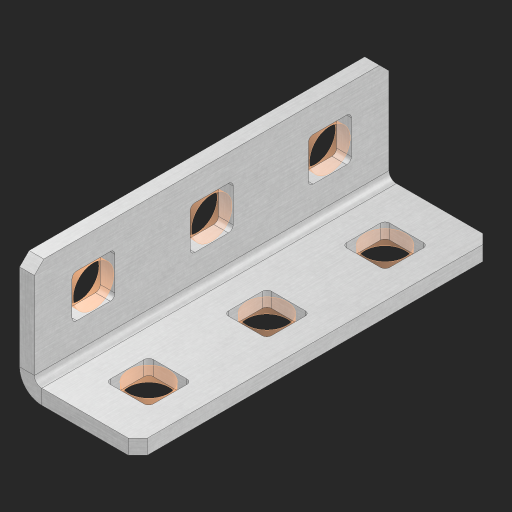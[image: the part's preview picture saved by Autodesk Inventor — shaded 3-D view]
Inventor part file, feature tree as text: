
AUTODESK INVENTOR PART (.ipt)
format: ipt  version: 2023 (Build 270158000, 158)  size: 484,864 bytes
history: native  units: in
note: dims shown in document units (in); Inventor stores cm internally (conversion verified against a paired STEP export)
features: other x12, sheet_metal_op x8, extrude x7, sketch x5, pattern_linear x1, mirror x1, chamfer x1
ambient origin geometry x8: Origin, YZ Plane, XZ Plane, XY Plane, X Axis, Y Axis, Z Axis, Center Point
bodies: Solid1 (feature_tree), Body (feature_tree)
feature tree (35):
  sheet_metal_op  "Flanges"
  sheet_metal_op  "Body Pattern"
  other  "Arc Length"
  pattern_linear  "Notch Pattern"  Spacing1=0.125in  [1 undecoded]
  other  "Diagonal Plane"
  mirror  "Everything Mirrored"
  chamfer  "End Chamfer"
  sketch  "Sketch1"  dims[d0=0.5in]
  other  "Plate1"
  sketch  "Sketch2"  dims[d1=1.5in]
  other  "Plate2"
  sheet_metal_op  "Bend1"
  sheet_metal_op  "Corner1"
  sketch  "Sketch8"  dims[d2=0.0625in]
  sketch  "Sketch9"  dims[d3=0.0625in]
  other  "Srf91"
  sheet_metal_op  "Body Pattern Sketch"
  other  "Srf92"
  sketch  "Sketch13"  dims[d4=0.0312in d5=0.125in d6=0.0625in d7=0.5in d8=90.0deg d9=0.0312in d10=0.25in d11=0.0625in d12=0.0625in d49=0.182in d50=0.02in d52=0.25in d53=0.0625in d54=0.0in d55=0.172in d56=1.0in d57=0.0in d85=0.1473in d86=0.1782in d89=0.0625in d90=0.0in d91=0.04in d92=0.0491in d95=2.5in d96=0.04in d97=0.25in d98=45.0deg d123=0.204in d126=0.0491in d127=0.1473in d128=0.08in d129=0.04in d130=2.5in d131=1.1811in d133=0.5in d134=0.3937in d136=1.0in]
  other  "Srf856"
  other  "Srf857"
  other  "Srf1275"
  other  "Srf1276"
  other  "Srf1278"
  other  "Srf1279"
  sheet_metal_op  "Body Stamp"
  sheet_metal_op  "Body Circle"
  sheet_metal_op  "Notch"
  extrude  "ExtrusionSrf92"  Depth=0.0625in
  extrude  "ExtrusionSrf856"  Depth=0.5in TaperAngle=90.0deg
  extrude  "ExtrusionSrf857"  Depth=0.25in
  extrude  "ExtrusionSrf1275"  Depth=0.0625in
  extrude  "ExtrusionSrf1276"  Depth=0.0625in
  extrude  "ExtrusionSrf1277"  Depth=0.182in
  extrude  "ExtrusionSrf1278"  Depth=0.02in
note: 1 required parameter value undecoded (feature->parameter linkage not recoverable at this tier; creation-order binding heuristic only, values carry confidence <= 0.55)
